# Revit family: Towel_Bar-Single-Symmons-Dia
name_source: partatom
category: Furniture
revit_build: Autodesk Revit 2015 (Build: 20140606_1530(x64)
units: mm (PartAtom-declared; Revit-internal decimal feet)

## types (4) — shared parameters
Date Modified = January 30, 2015
Default Elevation = 48 "
Equipment Abbreviation = TB
Family Version = 1.0
Manufacturer = Symmons Industries, Inc.
Model Disclaimer = Contact Symmons Industries, Inc. For More Information
Product Documentation Link = http://www.symmons.com
Product Page URL = http://www.symmons.com
Product data url = https://bimobject.com
URL = http://www.symmons.com

## per-type parameters (varying)
| type | Description | Model | Product Material | z Type Length | z Type Material |
| 18", Chrome | Towel Bar, 18 Inch, Chrome | 353TB-18 | Chrome - Symmons - Polished | 18 | 1 |
| 18", Satin Nickel | Towel Bar, 18 Inch, Satin Nickel | 353TB-18-STN | Nickel - Symmons - Satin | 18 | 2 |
| 24", Satin Nickel | Towel Bar, 24 Inch, Satin Nickel | 353TB-24-STN | Nickel - Symmons - Satin | 24 | 2 |
| 24", Chrome | Towel Bar, 24 Inch, Chrome | 353TB-24 | Chrome - Symmons - Polished | 24 | 1 |

## geometry (parser evidence)
native form markers: Blend x2, Sweep x2
no freeform markers — native parametric forms only
